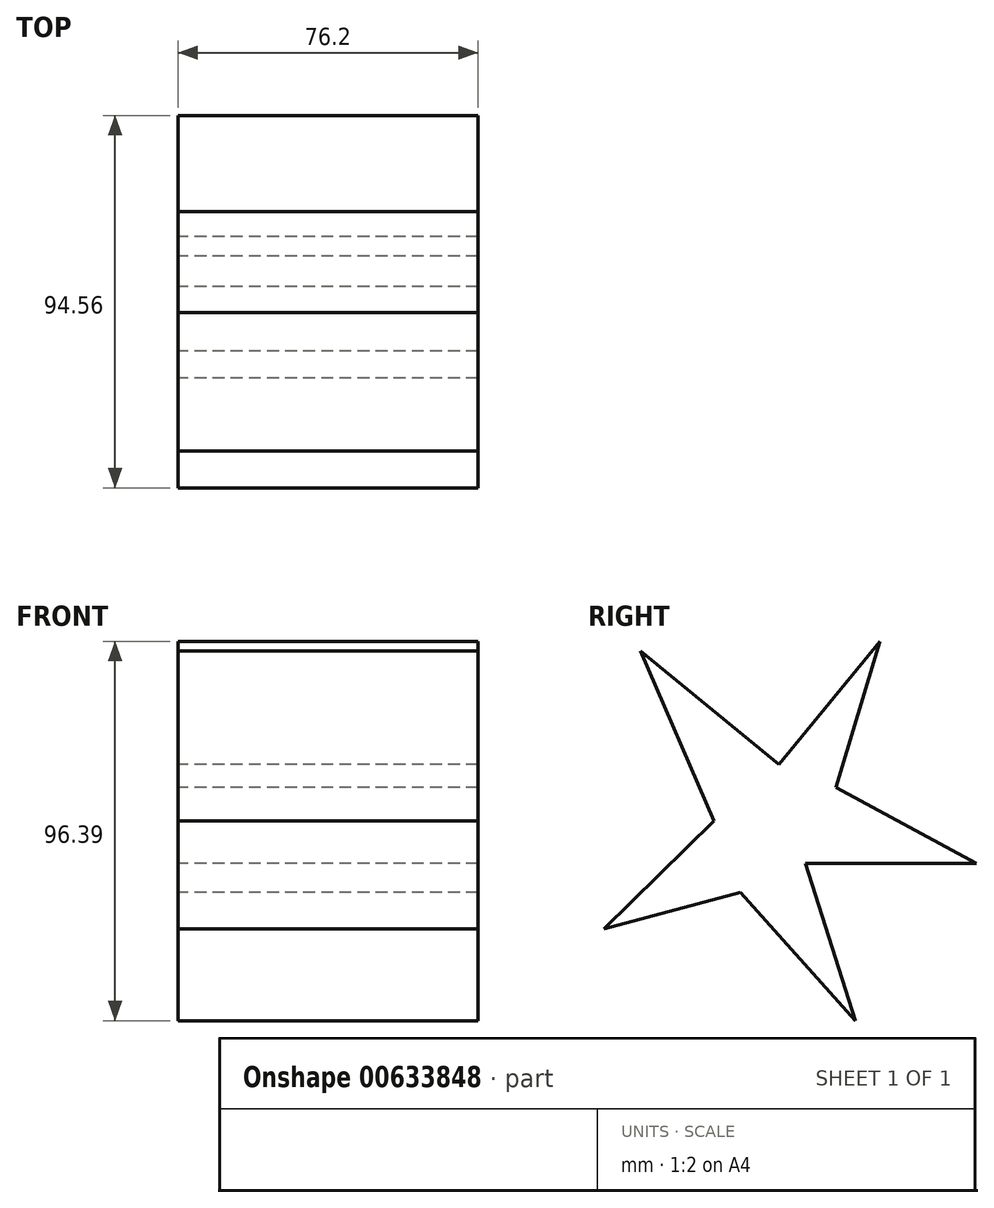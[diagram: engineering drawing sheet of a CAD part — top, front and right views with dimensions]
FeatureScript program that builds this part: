
annotation { "Feature Type Name" : "Feature", "Feature Type Description" : "" }
export const myFeature = defineFeature(function(context is Context, id is Id, definition is map)
    precondition{}
    {
        {
            var Q0;
            Q0=qCreatedBy(makeId("Right.planeOp"),FACE);
            var sketch = newSketch(context, id + "F0", { "sketchPlane" : qUnion([Q0])});
            skLineSegment(sketch, "E0", {"start": v(-35.19, 43.26) * mm, "end": v(0, 14.42) * mm});
            skLineSegment(sketch, "E1", {"start": v(0, 14.42) * mm, "end": v(25.63, 45.7) * mm});
            skLineSegment(sketch, "E2", {"start": v(25.63, 45.7) * mm, "end": v(14.42, 8.53) * mm});
            skLineSegment(sketch, "E3", {"start": v(14.42, 8.53) * mm, "end": v(50.07, -10.7) * mm});
            skLineSegment(sketch, "E4", {"start": v(50.07, -10.7) * mm, "end": v(6.67, -10.7) * mm});
            skLineSegment(sketch, "E5", {"start": v(6.67, -10.7) * mm, "end": v(19.38, -50.69) * mm});
            skLineSegment(sketch, "E6", {"start": v(19.38, -50.69) * mm, "end": v(-9.77, -18.13) * mm});
            skLineSegment(sketch, "E7", {"start": v(-9.77, -18.13) * mm, "end": v(-44.5, -27.43) * mm});
            skLineSegment(sketch, "E8", {"start": v(-44.5, -27.43) * mm, "end": v(-16.59, 0) * mm});
            skLineSegment(sketch, "E9", {"start": v(-16.59, 0) * mm, "end": v(-35.19, 43.26) * mm});
            skSolve(sketch);
        }
        {
            var Q0;
            Q0=makeQuery(id+"F0.imprint","IMPRINT",FACE,{"disambiguationData":[TD([[makeQuery(id+"F0.imprint","IMPRINT",EDGE,{"derivedFrom":sQuery(id+"F0.wireOp",EDGE,"E0")}),-1.0]])]});
            extrude(context, id + "F1", {"entities" : qUnion([Q0]), "depth" : 76.2 * mm, "offsetDistance" : 25.4 * mm});
        }
    });
